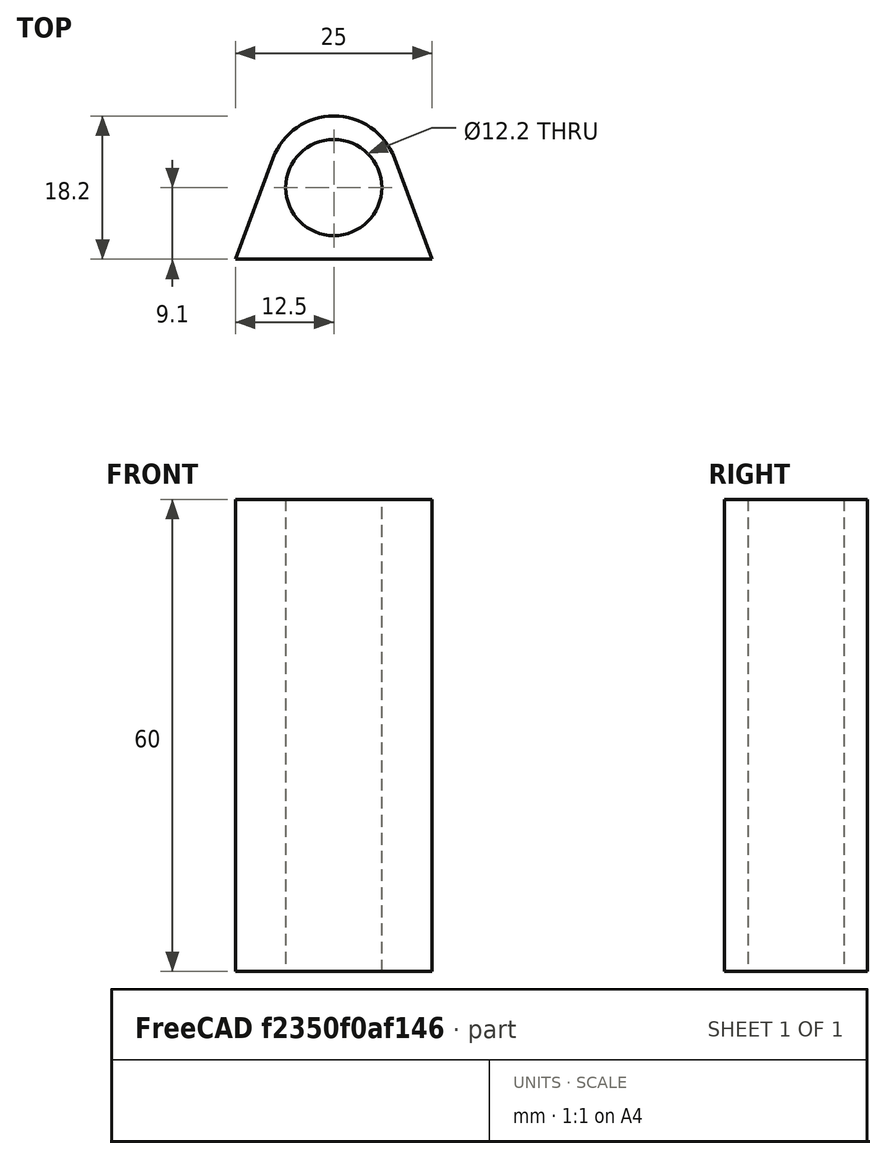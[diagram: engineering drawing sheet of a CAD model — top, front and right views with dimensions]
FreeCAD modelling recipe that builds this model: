
FCSTD DOCUMENT  (FreeCAD 2022.111R30764 (Git))
Label: door opener small pir floor mount
License: All rights reserved
LicenseURL: http://en.wikipedia.org/wiki/All_rights_reserved
objects: Sketcher::SketchObject×1, PartDesign::Pad×1, PartDesign::Body×1
note: 5 computed .brp shape members not serialized (recipe doc carries the construction recipe); baked Part::Feature solids carry a one-line shape summary decoded from their .brp

FEATURE [Sketcher::SketchObject] Sketch
  FullyConstrained = true
  MapMode = 5
  Support = -> [XY_Plane]
  TreeRank = 11
  sketch-geometry (13):
    g0: Circle CenterX=0 CenterY=0 CenterZ=0 NormalX=0 NormalY=0 NormalZ=1 AngleXU=0 Radius=6.1
    g1: LineSegment StartX=-7.69497 StartY=3.76052 StartZ=0 EndX=-12.5 EndY=-9.1 EndZ=0
    g2: LineSegment StartX=-12.5 StartY=-9.1 StartZ=0 EndX=12.5 EndY=-9.1 EndZ=0
    g3: LineSegment StartX=12.5 StartY=-9.1 StartZ=0 EndX=7.69497 EndY=3.76052 EndZ=0
    g4: ArcOfCircle CenterX=-1.54e-14 CenterY=0.885472 CenterZ=0 NormalX=0 NormalY=0 NormalZ=1 AngleXU=0 Radius=8.21453 StartAngle=0.357566 EndAngle=2.78403
    g5: GeomPoint [constr] X=0 Y=24.3559 Z=0
    g6: GeomPoint [constr] X=-9.1 Y=0 Z=0
    g7: GeomPoint [constr] X=9.1 Y=0 Z=0
    g8: GeomPoint [constr] X=0 Y=9.1 Z=0
    g9: GeomPoint [constr] X=0 Y=6.1 Z=0
    g10: GeomPoint [constr] X=0 Y=-6.1 Z=0
    g11: GeomPoint [constr] X=0 Y=-9.1 Z=0
    g12: GeomPoint [constr] X=-6.1 Y=0 Z=0
  constraints (28):
    c: Coincident(g0,g-1)
    c: Diameter(g0) = 12.2
    c: PointOnObject(g5,g-2)
    c: Coincident(g1,g2)
    c: Horizontal(g2)
    c: Coincident(g2,g3)
    c: PointOnObject(g5,g1)
    c: PointOnObject(g5,g3)
    c: Tangent(g1,g4) = -1.5708
    c: Tangent(g3,g4) = -1.5708
    c: PointOnObject(g6,g1)
    c: PointOnObject(g7,g3)
    c: Symmetric(g7,g6,g-2)
    c: PointOnObject(g6,g-1)
    c: PointOnObject(g8,g4)
    c: PointOnObject(g9,g0)
    c: PointOnObject(g8,g-2)
    c: PointOnObject(g9,g-2)
    c: DistanceY(g9,g8) = 3
    c: PointOnObject(g10,g0)
    c: PointOnObject(g11,g2)
    c: PointOnObject(g10,g-2)
    c: PointOnObject(g11,g-2)
    c: DistanceY(g11,g10) = 3
    c: PointOnObject(g12,g0)
    c: PointOnObject(g12,g-1)
    c: DistanceX(g6,g12) = 3
    c: DistanceX(g2,g2) = 25
FEATURE [PartDesign::Pad] Pad
  AddSubType = 0
  AlongSketchNormal = false
  CheckUpToFaceLimits = true
  ClaimChildren = false
  Direction = (0,0,1)
  Fit = 0
  FitJoin = 0
  InnerFit = 0
  InnerFitJoin = 0
  InnerTaperAngle = 0
  InnerTaperAngleRev = 0
  Length = 60
  Length2 = 100
  Linearize = true
  NewSolid = false
  Profile = -> Sketch
  Suppress = false
  TreeRank = 12
  Type = 0
  _ProfileBasedVersion = 1
FEATURE [PartDesign::Body] Body
  AutoGroupSolids = false
  ExportMode = 0
  Group = -> [Sketch,Pad]
  Origin = -> Origin
  Tip = -> Pad
  TreeRank = 10
  _ExportChildren = -> [Pad]
  _GroupVersion = 1
